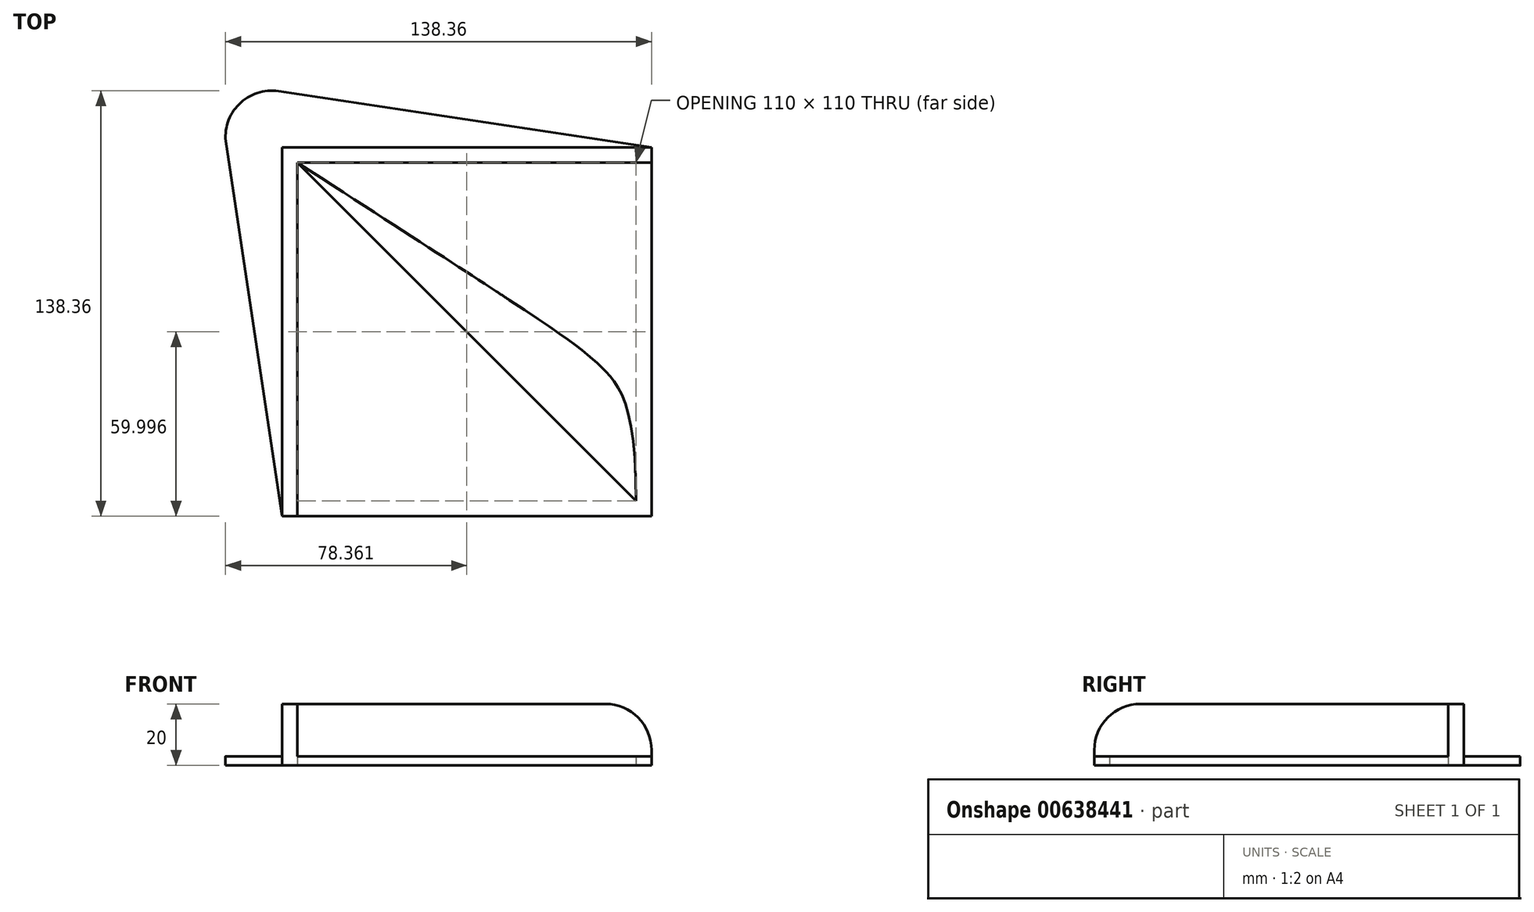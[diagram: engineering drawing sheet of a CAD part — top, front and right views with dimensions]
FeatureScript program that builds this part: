
annotation { "Feature Type Name" : "Feature", "Feature Type Description" : "" }
export const myFeature = defineFeature(function(context is Context, id is Id, definition is map)
    precondition{}
    {
        {
            var Q0;
            Q0=qCreatedBy(makeId("Top.planeOp"),FACE);
            var sketch = newSketch(context, id + "F0", { "sketchPlane" : qUnion([Q0])});
            skLineSegment(sketch, "E0.bottom", {"start": v(-63.23, 46.89) * mm, "end": v(56.77, 46.89) * mm});
            skLineSegment(sketch, "E0.top", {"start": v(-63.23, -73.11) * mm, "end": v(56.77, -73.11) * mm});
            skLineSegment(sketch, "E0.left", {"start": v(-63.23, 46.89) * mm, "end": v(-63.23, -73.11) * mm});
            skLineSegment(sketch, "E0.right", {"start": v(56.77, 46.89) * mm, "end": v(56.77, -73.11) * mm});
            skLineSegment(sketch, "E1", {"start": v(-63.23, 46.89) * mm, "end": v(56.77, -73.11) * mm});
            skLineSegment(sketch, "E2.0", {"start": v(-58.23, 41.89) * mm, "end": v(51.77, 41.89) * mm});
            skLineSegment(sketch, "E2.1", {"start": v(-58.23, 41.89) * mm, "end": v(-58.23, -68.11) * mm});
            skLineSegment(sketch, "E2.2", {"start": v(-58.23, -68.11) * mm, "end": v(51.77, -68.11) * mm});
            skLineSegment(sketch, "E2.3", {"start": v(51.77, 41.89) * mm, "end": v(51.77, -68.11) * mm});
            skLineSegment(sketch, "E3", {"start": v(-63.23, 46.89) * mm, "end": v(-84.44, 68.1) * mm});
            skLineSegment(sketch, "E4", {"start": v(-84.44, 68.1) * mm, "end": v(-63.23, -73.11) * mm});
            skLineSegment(sketch, "E5", {"start": v(-84.44, 68.1) * mm, "end": v(56.77, 46.89) * mm});
            skLineSegment(sketch, "E6", {"start": v(-58.23, -68.11) * mm, "end": v(-58.23, -73.11) * mm});
            skLineSegment(sketch, "E7", {"start": v(51.77, 41.89) * mm, "end": v(56.77, 41.89) * mm});
            skFitSpline(sketch, "E8", {"points": [v(-58.23, 41.89) * mm, v(40.91, -25.02) * mm, v(51.77, -68.11) * mm], "startDerivative": vector(392.46, -254.2) * mm, "endDerivative": vector(0, -246.8) * mm});
            skLineSegment(sketch, "E9", {"start": v(-58.23, -64.58) * mm, "end": v(-5, -11.35) * mm});
            skLineSegment(sketch, "E10", {"start": v(-1.46, -14.88) * mm, "end": v(-54.7, -68.11) * mm});
            skLineSegment(sketch, "E11", {"start": v(6.35, 0) * mm, "end": v(48.24, 41.89) * mm});
            skLineSegment(sketch, "E12", {"start": v(51.77, 38.35) * mm, "end": v(10.62, -2.8) * mm});
            skSolve(sketch);
        }
        {
            var Q0;
            Q0=makeQuery(id+"F0.imprint","IMPRINT",FACE,{"disambiguationData":[TD([[makeQuery(id+"F0.imprint","IMPRINT",EDGE,{"derivedFrom":sQuery(id+"F0.wireOp",EDGE,"E0.bottom")}),1.0]])]});
            var Q1;
            Q1=makeQuery(id+"F0.imprint","IMPRINT",FACE,{"disambiguationData":[TD([[makeQuery(id+"F0.imprint","IMPRINT",EDGE,{"derivedFrom":sQuery(id+"F0.wireOp",EDGE,"E0.left")}),-1.0]])]});
            var Q2;
            {var subQ3=sQuery(id+"F0.wireOp",EDGE,"E9");Q2=makeQuery(id+"F0.imprint","IMPRINT",FACE,{"disambiguationData":[TD([[makeQuery(id+"F0.imprint","IMPRINT",EDGE,{"derivedFrom":subQ3}),1.0]])]});}
            var Q3;
            {var subQ3=sQuery(id+"F0.wireOp",EDGE,"E11");Q3=makeQuery(id+"F0.imprint","IMPRINT",FACE,{"disambiguationData":[TD([[makeQuery(id+"F0.imprint","IMPRINT",EDGE,{"derivedFrom":subQ3}),1.0]])]});}
            var Q4;
            {var subQ4=sQuery(id+"F0.wireOp",EDGE,"E0.bottom");Q4=makeQuery(id+"F0.imprint","IMPRINT",FACE,{"disambiguationData":[TD([[makeQuery(id+"F0.imprint","IMPRINT",EDGE,{"derivedFrom":subQ4}),-1.0]])]});}
            var Q5;
            {var subQ4=sQuery(id+"F0.wireOp",EDGE,"E0.left");Q5=makeQuery(id+"F0.imprint","IMPRINT",FACE,{"disambiguationData":[TD([[makeQuery(id+"F0.imprint","IMPRINT",EDGE,{"derivedFrom":subQ4}),1.0]])]});}
            var Q6;
            {var subQ0=sQuery(id+"F0.wireOp",EDGE,"E9");Q6=makeQuery(id+"F0.imprint","IMPRINT",FACE,{"disambiguationData":[TD([[makeQuery(id+"F0.imprint","IMPRINT",EDGE,{"derivedFrom":subQ0}),-1.0]])]});}
            var Q7;
            {var subQ3=sQuery(id+"F0.wireOp",EDGE,"E10");Q7=makeQuery(id+"F0.imprint","IMPRINT",FACE,{"disambiguationData":[TD([[makeQuery(id+"F0.imprint","IMPRINT",EDGE,{"derivedFrom":subQ3}),1.0]])]});}
            var Q8;
            {var subQ4=sQuery(id+"F0.wireOp",EDGE,"E6");Q8=makeQuery(id+"F0.imprint","IMPRINT",FACE,{"disambiguationData":[TD([[makeQuery(id+"F0.imprint","IMPRINT",EDGE,{"derivedFrom":subQ4}),1.0]])]});}
            var Q9;
            {var subQ4=sQuery(id+"F0.wireOp",EDGE,"E7");Q9=makeQuery(id+"F0.imprint","IMPRINT",FACE,{"disambiguationData":[TD([[makeQuery(id+"F0.imprint","IMPRINT",EDGE,{"derivedFrom":subQ4}),-1.0]])]});}
            var Q10;
            {var subQ3=sQuery(id+"F0.wireOp",EDGE,"E12");Q10=makeQuery(id+"F0.imprint","IMPRINT",FACE,{"disambiguationData":[TD([[makeQuery(id+"F0.imprint","IMPRINT",EDGE,{"derivedFrom":subQ3}),1.0]])]});}
            var Q11;
            {var subQ0=sQuery(id+"F0.wireOp",EDGE,"E11");Q11=makeQuery(id+"F0.imprint","IMPRINT",FACE,{"disambiguationData":[TD([[makeQuery(id+"F0.imprint","IMPRINT",EDGE,{"derivedFrom":subQ0}),-1.0]])]});}
            extrude(context, id + "F1", {"entities" : qUnion([Q0, Q1, Q2, Q3, Q4, Q5, Q6, Q7, Q8, Q9, Q10, Q11]), "depth" : 3 * mm, "offsetDistance" : 25 * mm});
        }
        {
            var Q0;
            {var subQ4=sQuery(id+"F0.wireOp",EDGE,"E0.bottom");Q0=makeQuery(id+"F0.imprint","IMPRINT",FACE,{"disambiguationData":[TD([[makeQuery(id+"F0.imprint","IMPRINT",EDGE,{"derivedFrom":subQ4}),-1.0]])]});}
            var Q1;
            {var subQ4=sQuery(id+"F0.wireOp",EDGE,"E0.left");Q1=makeQuery(id+"F0.imprint","IMPRINT",FACE,{"disambiguationData":[TD([[makeQuery(id+"F0.imprint","IMPRINT",EDGE,{"derivedFrom":subQ4}),1.0]])]});}
            extrude(context, id + "F2", {"entities" : qUnion([Q0, Q1]), "operationType" : NewBodyOperationType.ADD, "depth" : 20 * mm, "offsetDistance" : 25 * mm});
        }
        {
            var Q0;
            Q0=makeQuery(id+"F2.opExtrude","CAP_EDGE",EDGE,{"disambiguationData":[OSD([sQuery(id+"F0.wireOp",EDGE,"E0.top")])],"isStart":false});
            var Q1;
            Q1=makeQuery(id+"F2.opExtrude","CAP_EDGE",EDGE,{"disambiguationData":[OSD([sQuery(id+"F0.wireOp",EDGE,"E0.right")])],"isStart":false});
            var Q2;
            Q2=makeQuery(id+"F1.opExtrude","SWEPT_EDGE",EDGE,{"disambiguationData":[OSD([sQuery(id+"F0.wireOp",EDGE,"E3"),sQuery(id+"F0.wireOp",EDGE,"E4"),sQuery(id+"F0.wireOp",EDGE,"E5")])]});
            fillet(context, id + "F3", {"entities" : qUnion([Q0, Q1, Q2]), "radius" : 15 * mm, "tangentPropagation" : true, "allowEdgeOverflow" : false});
        }
    });
